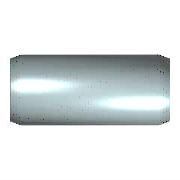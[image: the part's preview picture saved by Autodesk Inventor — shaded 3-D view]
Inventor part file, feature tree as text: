
AUTODESK INVENTOR PART (.ipt)
format: ipt  version: 2023.3 (Build 273359000, 359)  size: 113,152 bytes
history: native  units: mm (DEFAULTED — no unit token found)
features: extrude x1, chamfer x1, sketch x1
ambient origin geometry x8: Origin, YZ Plane, XZ Plane, XY Plane, X Axis, Y Axis, Z Axis, Center Point
bodies: Solid1 (feature_tree)
feature tree (3):
  extrude  "Körper"  Depth=20.0mm
  chamfer  "Skizze2"  [1 undecoded]
  sketch  "Skizze"  dims[d1=2.0mm d2=20.0mm d3=0.0mm d4=0.35mm d5=15.0deg d8=0.35mm d9=15.0deg d11=0.35mm d12=0.35mm d13=0.0mm d15=0.0mm d16=0.0mm]
note: 1 required parameter value undecoded (feature->parameter linkage not recoverable at this tier; creation-order binding heuristic only, values carry confidence <= 0.55)
